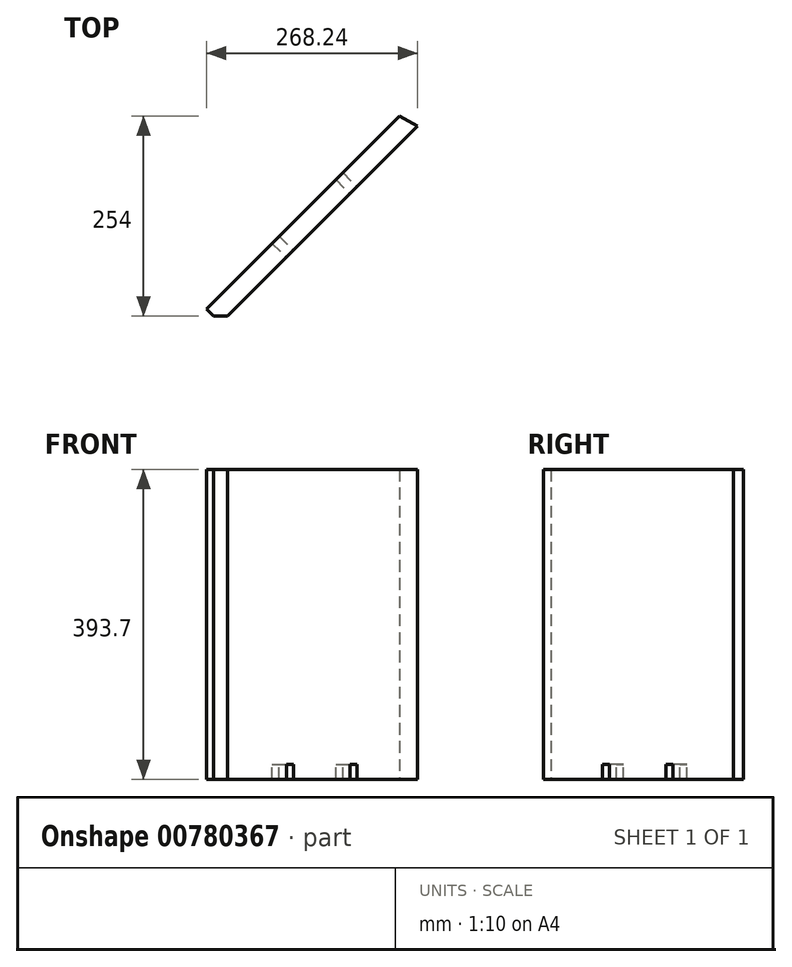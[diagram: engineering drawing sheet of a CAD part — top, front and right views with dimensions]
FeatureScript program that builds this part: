
annotation { "Feature Type Name" : "Feature", "Feature Type Description" : "" }
export const myFeature = defineFeature(function(context is Context, id is Id, definition is map)
    precondition{}
    {
        {
            var Q0;
            Q0=qCreatedBy(makeId("Top.planeOp"),FACE);
            var sketch = newSketch(context, id + "F0", { "sketchPlane" : qUnion([Q0])});
            skLineSegment(sketch, "E0", {"start": v(-279.89, 254) * mm, "end": v(278.91, 254) * mm});
            skLineSegment(sketch, "E1", {"start": v(278.91, 254) * mm, "end": v(532.91, 0) * mm});
            skLineSegment(sketch, "E2.MirrorCS", {"start": v(-279.89, -254) * mm, "end": v(278.91, -254) * mm});
            skLineSegment(sketch, "E3.MirrorCS", {"start": v(278.91, -254) * mm, "end": v(532.91, 0) * mm});
            skLineSegment(sketch, "E4.0", {"start": v(-288.87, 245.02) * mm, "end": v(-43.85, 0) * mm});
            skLineSegment(sketch, "E5.0", {"start": v(-261.93, 254) * mm, "end": v(-20.63, 12.7) * mm});
            skLineSegment(sketch, "E6.MirrorCS", {"start": v(-261.93, -254) * mm, "end": v(-20.63, -12.7) * mm});
            skLineSegment(sketch, "E7.MirrorCS", {"start": v(-288.87, -245.02) * mm, "end": v(-43.85, 0) * mm});
            skLineSegment(sketch, "E8.0", {"start": v(-20.63, -12.7) * mm, "end": v(520.21, -12.7) * mm});
            skLineSegment(sketch, "E9.0", {"start": v(-20.63, 12.7) * mm, "end": v(520.21, 12.7) * mm});
            skLineSegment(sketch, "E10", {"start": v(-43.85, 0) * mm, "end": v(-20.63, 12.7) * mm});
            skLineSegment(sketch, "E11", {"start": v(-43.85, 0) * mm, "end": v(-20.63, -12.7) * mm});
            skLineSegment(sketch, "E12", {"start": v(-115.7, -71.84) * mm, "end": v(-97.73, -89.8) * mm});
            skLineSegment(sketch, "E13.0", {"start": v(-124.67, -80.82) * mm, "end": v(-106.71, -98.78) * mm});
            skLineSegment(sketch, "E14", {"start": v(-279.89, 254) * mm, "end": v(-533.89, 0) * mm});
            skLineSegment(sketch, "E15", {"start": v(-533.89, 0) * mm, "end": v(-279.89, -254) * mm});
            skLineSegment(sketch, "E16", {"start": v(-533.89, 0) * mm, "end": v(532.91, 0) * mm, "construction": true});
            skLineSegment(sketch, "E17.MirrorCS", {"start": v(-124.67, 80.82) * mm, "end": v(-106.71, 98.78) * mm});
            skLineSegment(sketch, "E18.MirrorCS", {"start": v(-115.7, 71.84) * mm, "end": v(-97.73, 89.8) * mm});
            skLineSegment(sketch, "E19", {"start": v(80.97, 12.7) * mm, "end": v(80.97, -12.7) * mm});
            skLineSegment(sketch, "E20.0", {"start": v(93.67, 12.7) * mm, "end": v(93.67, -12.7) * mm});
            skLineSegment(sketch, "E21", {"start": v(-196.51, 152.66) * mm, "end": v(-178.55, 170.62) * mm});
            skLineSegment(sketch, "E22.0", {"start": v(-205.5, 161.64) * mm, "end": v(-187.53, 179.6) * mm});
            skLineSegment(sketch, "E23.MirrorCS", {"start": v(-196.51, -152.66) * mm, "end": v(-178.55, -170.62) * mm});
            skLineSegment(sketch, "E24.MirrorCS", {"start": v(-205.5, -161.64) * mm, "end": v(-187.53, -179.6) * mm});
            skSolve(sketch);
        }
        {
            var Q0;
            {var subQ0=sQuery(id+"F0.wireOp",EDGE,"E13.0");Q0=makeQuery(id+"F0.imprint","IMPRINT",FACE,{"disambiguationData":[TD([[makeQuery(id+"F0.imprint","IMPRINT",EDGE,{"derivedFrom":subQ0}),-1.0]])]});}
            var Q1;
            {var subQ0=sQuery(id+"F0.wireOp",EDGE,"E11");Q1=makeQuery(id+"F0.imprint","IMPRINT",FACE,{"disambiguationData":[TD([[makeQuery(id+"F0.imprint","IMPRINT",EDGE,{"derivedFrom":subQ0}),-1.0]])]});}
            var Q2;
            {var subQ0=sQuery(id+"F0.wireOp",EDGE,"E12");Q2=makeQuery(id+"F0.imprint","IMPRINT",FACE,{"disambiguationData":[TD([[makeQuery(id+"F0.imprint","IMPRINT",EDGE,{"derivedFrom":subQ0}),-1.0]])]});}
            var Q3;
            {var subQ5=sQuery(id+"F0.wireOp",EDGE,"E24.MirrorCS");Q3=makeQuery(id+"F0.imprint","IMPRINT",FACE,{"disambiguationData":[TD([[makeQuery(id+"F0.imprint","IMPRINT",EDGE,{"derivedFrom":subQ5}),-1.0]])]});}
            var Q4;
            {var subQ0=sQuery(id+"F0.wireOp",EDGE,"E23.MirrorCS");Q4=makeQuery(id+"F0.imprint","IMPRINT",FACE,{"disambiguationData":[TD([[makeQuery(id+"F0.imprint","IMPRINT",EDGE,{"derivedFrom":subQ0}),-1.0]])]});}
            var Q5;
            Q5=sQuery(id+"F0.wireOp",EDGE,"E7.MirrorCS");
            var Q6;
            Q6=sQuery(id+"F0.wireOp",EDGE,"E6.MirrorCS");
            extrude(context, id + "F1", {"entities" : qUnion([Q0, Q1, Q2, Q3, Q4]), "surfaceEntities" : qUnion([Q5, Q6]), "depth" : 374.65 * mm, "offsetDistance" : 25.4 * mm});
        }
        {
            var Q0;
            {var subQ0=sQuery(id+"F0.wireOp",EDGE,"E11");Q0=makeQuery(id+"F0.imprint","IMPRINT",FACE,{"disambiguationData":[TD([[makeQuery(id+"F0.imprint","IMPRINT",EDGE,{"derivedFrom":subQ0}),-1.0]])]});}
            var Q1;
            {var subQ0=sQuery(id+"F0.wireOp",EDGE,"E13.0");Q1=makeQuery(id+"F0.imprint","IMPRINT",FACE,{"disambiguationData":[TD([[makeQuery(id+"F0.imprint","IMPRINT",EDGE,{"derivedFrom":subQ0}),-1.0]])]});}
            var Q2;
            {var subQ5=sQuery(id+"F0.wireOp",EDGE,"E24.MirrorCS");Q2=makeQuery(id+"F0.imprint","IMPRINT",FACE,{"disambiguationData":[TD([[makeQuery(id+"F0.imprint","IMPRINT",EDGE,{"derivedFrom":subQ5}),-1.0]])]});}
            extrude(context, id + "F2", {"entities" : qUnion([Q0, Q1, Q2]), "operationType" : NewBodyOperationType.ADD, "oppositeDirection" : true, "depth" : 19.05 * mm, "offsetDistance" : 25.4 * mm});
        }
    });
